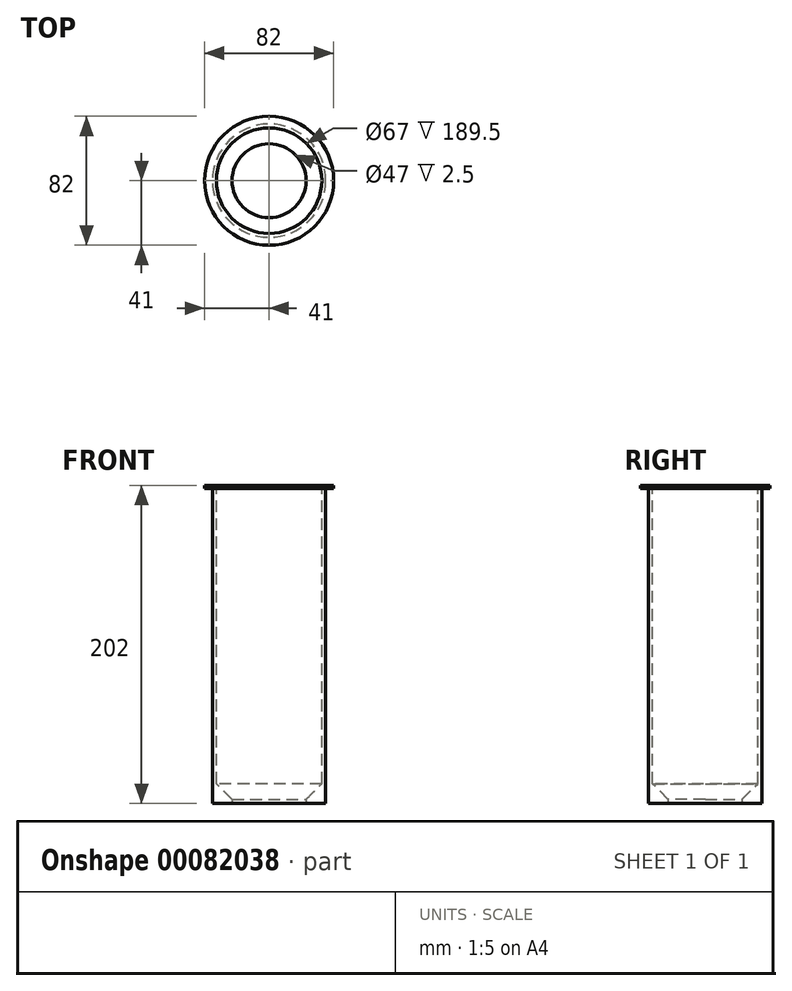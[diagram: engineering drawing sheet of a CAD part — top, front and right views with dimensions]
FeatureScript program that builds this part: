
annotation { "Feature Type Name" : "Feature", "Feature Type Description" : "" }
export const myFeature = defineFeature(function(context is Context, id is Id, definition is map)
    precondition{}
    {
        {
            var Q0;
            Q0=qCreatedBy(makeId("Top.planeOp"),FACE);
            var sketch = newSketch(context, id + "F0", { "sketchPlane" : qUnion([Q0])});
            skCircle(sketch, "E0", {"center": v(0, 0) * mm, "radius": 41 * mm});
            skCircle(sketch, "E1", {"center": v(0, 0) * mm, "radius": 36 * mm});
            skSolve(sketch);
        }
        {
            var Q0;
            Q0=makeQuery(id+"F0.imprint","IMPRINT",FACE,{"disambiguationData":[TD([[makeQuery(id+"F0.imprint","IMPRINT",EDGE,{"derivedFrom":sQuery(id+"F0.wireOp",EDGE,"E1")}),1.0]])]});
            var Q1;
            Q1=makeQuery(id+"F0.imprint","IMPRINT",FACE,{"disambiguationData":[TD([[makeQuery(id+"F0.imprint","IMPRINT",EDGE,{"derivedFrom":sQuery(id+"F0.wireOp",EDGE,"E0")}),1.0]])]});
            extrude(context, id + "F1", {"entities" : qUnion([Q0, Q1]), "depth" : 2 * mm});
        }
        {
            var Q0;
            Q0=makeQuery(id+"F0.imprint","IMPRINT",FACE,{"disambiguationData":[TD([[makeQuery(id+"F0.imprint","IMPRINT",EDGE,{"derivedFrom":sQuery(id+"F0.wireOp",EDGE,"E1")}),1.0]])]});
            extrude(context, id + "F2", {"entities" : qUnion([Q0]), "operationType" : NewBodyOperationType.ADD, "oppositeDirection" : true, "depth" : 200 * mm});
        }
        {
            var Q0;
            Q0=makeQuery(id+"F1.opExtrude","CAP_FACE",FACE,{"disambiguationData":[OSD([sQuery(id+"F0.wireOp",EDGE,"E0")])],"isStart":false});
            shell(context, id + "F3", {"entities" : qUnion([Q0]), "thickness" : 2.5 * mm});
        }
        {
            var Q0;
            Q0=makeQuery(id+"F2.opExtrude","CAP_FACE",FACE,{"disambiguationData":[OSD([sQuery(id+"F0.wireOp",EDGE,"E1")])],"isStart":false});
            cPlane(context, id + "F4", {"entities" : qUnion([Q0]), "cplaneType" : CPlaneType.OFFSET, "offset" : 0 * mm, "width" : 150 * mm, "height" : 150 * mm});
        }
        {
            var Q0;
            Q0=qCreatedBy(id+"F4.planeOp",FACE);
            var sketch = newSketch(context, id + "F5", { "sketchPlane" : qUnion([Q0])});
            skCircle(sketch, "E2", {"center": v(0, 0) * mm, "radius": 23.5 * mm});
            skSolve(sketch);
        }
        {
            var Q0;
            Q0=makeQuery(id+"F5.imprint","IMPRINT",FACE,{"disambiguationData":[TD([[makeQuery(id+"F5.imprint","IMPRINT",EDGE,{"derivedFrom":sQuery(id+"F5.wireOp",EDGE,"E2")}),1.0]])]});
            extrude(context, id + "F6", {"entities" : qUnion([Q0]), "operationType" : NewBodyOperationType.REMOVE, "oppositeDirection" : true, "depth" : 25 * mm});
        }
        {
            var Q0;
            Q0=makeQuery(id+"F3.opShell","OFFSET_EDGE",EDGE,{"disambiguationData":[OSD([sQuery(id+"F0.wireOp",EDGE,"E1")])]});
            chamfer(context, id + "F7", {"entities" : qUnion([Q0]), "width" : 10 * mm, "tangentPropagation" : true});
        }
    });
